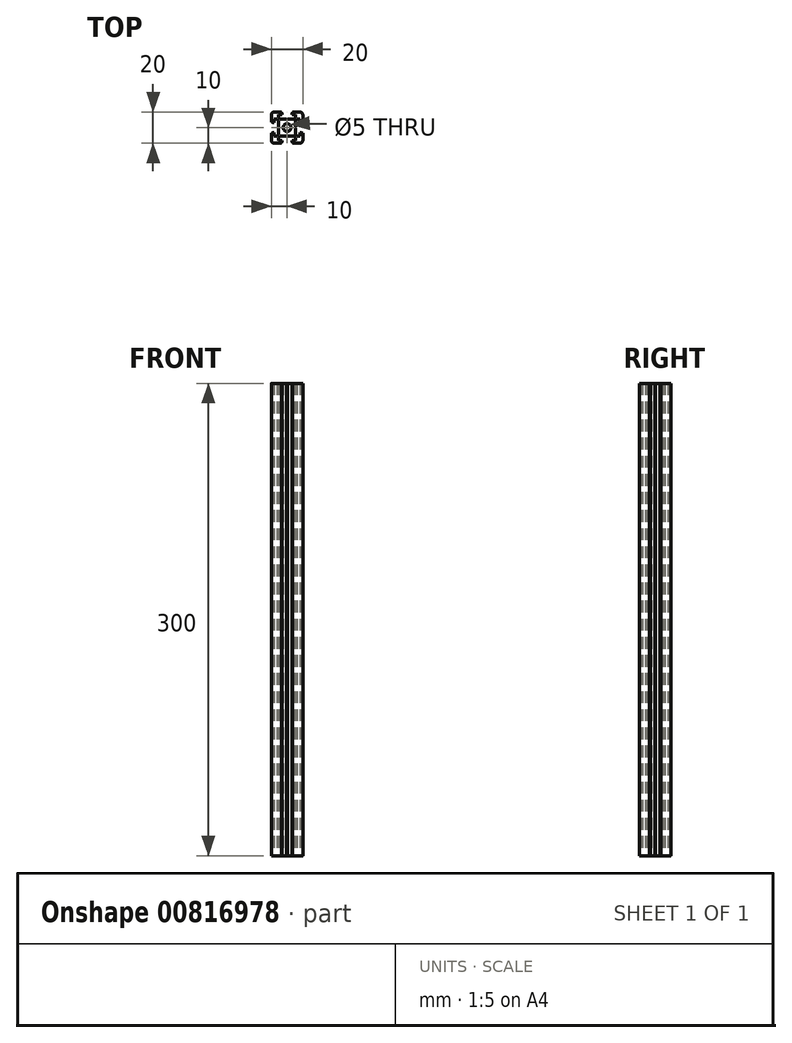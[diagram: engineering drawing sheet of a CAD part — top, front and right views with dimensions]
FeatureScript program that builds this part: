
annotation { "Feature Type Name" : "Feature", "Feature Type Description" : "" }
export const myFeature = defineFeature(function(context is Context, id is Id, definition is map)
    precondition{}
    {
        {
            var Q0;
            Q0=qCreatedBy(makeId("Top.planeOp"),FACE);
            var sketch = newSketch(context, id + "F0", { "sketchPlane" : qUnion([Q0])});
            skLineSegment(sketch, "E0.bottom", {"start": v(8, 10) * mm, "end": v(3.6, 10) * mm});
            skPoint(sketch, "E0.middle", {"position": v(0, 0) * mm});
            skLineSegment(sketch, "E1.bottom", {"start": v(4.58, 5.43) * mm, "end": v(0.25, 5.43) * mm});
            skLineSegment(sketch, "E2", {"start": v(-10, 10) * mm, "end": v(10, -10) * mm, "construction": true});
            skLineSegment(sketch, "E3", {"start": v(10, 10) * mm, "end": v(-10, -10) * mm, "construction": true});
            skLineSegment(sketch, "E4", {"start": v(-3.6, 10) * mm, "end": v(-3.6, 9.1) * mm});
            skLineSegment(sketch, "E5", {"start": v(-3.6, 9.1) * mm, "end": v(-3.1, 9.1) * mm});
            skLineSegment(sketch, "E6", {"start": v(-3.1, 9.1) * mm, "end": v(-3.1, 8.2) * mm});
            skLineSegment(sketch, "E7", {"start": v(-3.1, 8.2) * mm, "end": v(-5.45, 8.2) * mm});
            skLineSegment(sketch, "E8", {"start": v(-5.45, 8.2) * mm, "end": v(-5.45, 6.3) * mm});
            skLineSegment(sketch, "E9", {"start": v(-5.45, 6.3) * mm, "end": v(-4.58, 5.43) * mm});
            skLineSegment(sketch, "E10.MirrorCS", {"start": v(5.45, 8.2) * mm, "end": v(5.45, 6.3) * mm});
            skLineSegment(sketch, "E11.MirrorCS", {"start": v(3.1, 9.1) * mm, "end": v(3.1, 8.2) * mm});
            skLineSegment(sketch, "E12.MirrorCS", {"start": v(3.6, 10) * mm, "end": v(3.6, 9.1) * mm});
            skLineSegment(sketch, "E13.MirrorCS", {"start": v(3.1, 8.2) * mm, "end": v(5.45, 8.2) * mm});
            skLineSegment(sketch, "E14.MirrorCS", {"start": v(3.6, 9.1) * mm, "end": v(3.1, 9.1) * mm});
            skLineSegment(sketch, "E15.MirrorCS", {"start": v(5.45, 6.3) * mm, "end": v(4.58, 5.43) * mm});
            skPoint(sketch, "E16.visualSharp", {"position": v(-10, 10) * mm});
            skPoint(sketch, "E17.visualSharp", {"position": v(10, 10) * mm});
            skLineSegment(sketch, "E18.trimOffspring", {"start": v(-3.6, 10) * mm, "end": v(-8, 10) * mm});
            skLineSegment(sketch, "E19.1.0", {"start": v(-8.2, -3.1) * mm, "end": v(-8.2, -5.45) * mm});
            skLineSegment(sketch, "E19.1.2", {"start": v(-8.2, 5.45) * mm, "end": v(-6.3, 5.45) * mm});
            skLineSegment(sketch, "E19.1.3", {"start": v(-8.2, 3.1) * mm, "end": v(-8.2, 5.45) * mm});
            skPoint(sketch, "E19.1.4", {"position": v(-10, -10) * mm});
            skLineSegment(sketch, "E19.1.5", {"start": v(-9.1, -3.1) * mm, "end": v(-8.2, -3.1) * mm});
            skLineSegment(sketch, "E19.1.6", {"start": v(-6.3, 5.45) * mm, "end": v(-5.43, 4.58) * mm});
            skLineSegment(sketch, "E19.1.7", {"start": v(-5.43, 4.58) * mm, "end": v(-5.43, 0.25) * mm});
            skLineSegment(sketch, "E19.1.8", {"start": v(-8.2, -5.45) * mm, "end": v(-6.3, -5.45) * mm});
            skLineSegment(sketch, "E19.1.9", {"start": v(-9.1, 3.1) * mm, "end": v(-8.2, 3.1) * mm});
            skLineSegment(sketch, "E19.1.10", {"start": v(-6.3, -5.45) * mm, "end": v(-5.43, -4.58) * mm});
            skLineSegment(sketch, "E19.1.11", {"start": v(-10, 8) * mm, "end": v(-10, 3.6) * mm});
            skLineSegment(sketch, "E19.1.12", {"start": v(-10, -3.6) * mm, "end": v(-10, -8) * mm});
            skLineSegment(sketch, "E19.1.13", {"start": v(-10, 3.6) * mm, "end": v(-9.1, 3.6) * mm});
            skLineSegment(sketch, "E19.1.14", {"start": v(-9.1, -3.6) * mm, "end": v(-9.1, -3.1) * mm});
            skLineSegment(sketch, "E19.1.15", {"start": v(-10, -3.6) * mm, "end": v(-9.1, -3.6) * mm});
            skLineSegment(sketch, "E19.1.16", {"start": v(-9.1, 3.6) * mm, "end": v(-9.1, 3.1) * mm});
            skLineSegment(sketch, "E19.2.0", {"start": v(3.1, -8.2) * mm, "end": v(5.45, -8.2) * mm});
            skPoint(sketch, "E19.2.1", {"position": v(-10, -10) * mm});
            skLineSegment(sketch, "E19.2.2", {"start": v(-5.45, -8.2) * mm, "end": v(-5.45, -6.3) * mm});
            skLineSegment(sketch, "E19.2.3", {"start": v(-3.1, -8.2) * mm, "end": v(-5.45, -8.2) * mm});
            skPoint(sketch, "E19.2.4", {"position": v(10, -10) * mm});
            skLineSegment(sketch, "E19.2.5", {"start": v(3.1, -9.1) * mm, "end": v(3.1, -8.2) * mm});
            skLineSegment(sketch, "E19.2.6", {"start": v(-5.45, -6.3) * mm, "end": v(-4.58, -5.43) * mm});
            skLineSegment(sketch, "E19.2.7", {"start": v(-4.58, -5.43) * mm, "end": v(-0.25, -5.43) * mm});
            skLineSegment(sketch, "E19.2.8", {"start": v(5.45, -8.2) * mm, "end": v(5.45, -6.3) * mm});
            skLineSegment(sketch, "E19.2.9", {"start": v(-3.1, -9.1) * mm, "end": v(-3.1, -8.2) * mm});
            skLineSegment(sketch, "E19.2.10", {"start": v(5.45, -6.3) * mm, "end": v(4.58, -5.43) * mm});
            skLineSegment(sketch, "E19.2.11", {"start": v(-8, -10) * mm, "end": v(-3.6, -10) * mm});
            skLineSegment(sketch, "E19.2.12", {"start": v(3.6, -10) * mm, "end": v(8, -10) * mm});
            skLineSegment(sketch, "E19.2.13", {"start": v(-3.6, -10) * mm, "end": v(-3.6, -9.1) * mm});
            skLineSegment(sketch, "E19.2.14", {"start": v(3.6, -9.1) * mm, "end": v(3.1, -9.1) * mm});
            skLineSegment(sketch, "E19.2.15", {"start": v(3.6, -10) * mm, "end": v(3.6, -9.1) * mm});
            skLineSegment(sketch, "E19.2.16", {"start": v(-3.6, -9.1) * mm, "end": v(-3.1, -9.1) * mm});
            skLineSegment(sketch, "E19.3.0", {"start": v(8.2, 3.1) * mm, "end": v(8.2, 5.45) * mm});
            skPoint(sketch, "E19.3.1", {"position": v(10, -10) * mm});
            skLineSegment(sketch, "E19.3.2", {"start": v(8.2, -5.45) * mm, "end": v(6.3, -5.45) * mm});
            skLineSegment(sketch, "E19.3.3", {"start": v(8.2, -3.1) * mm, "end": v(8.2, -5.45) * mm});
            skLineSegment(sketch, "E19.3.5", {"start": v(9.1, 3.1) * mm, "end": v(8.2, 3.1) * mm});
            skLineSegment(sketch, "E19.3.6", {"start": v(6.3, -5.45) * mm, "end": v(5.43, -4.58) * mm});
            skLineSegment(sketch, "E19.3.7", {"start": v(5.43, -4.58) * mm, "end": v(5.43, -0.25) * mm});
            skLineSegment(sketch, "E19.3.8", {"start": v(8.2, 5.45) * mm, "end": v(6.3, 5.45) * mm});
            skLineSegment(sketch, "E19.3.9", {"start": v(9.1, -3.1) * mm, "end": v(8.2, -3.1) * mm});
            skLineSegment(sketch, "E19.3.10", {"start": v(6.3, 5.45) * mm, "end": v(5.43, 4.58) * mm});
            skLineSegment(sketch, "E19.3.11", {"start": v(10, -8) * mm, "end": v(10, -3.6) * mm});
            skLineSegment(sketch, "E19.3.12", {"start": v(10, 3.6) * mm, "end": v(10, 8) * mm});
            skLineSegment(sketch, "E19.3.13", {"start": v(10, -3.6) * mm, "end": v(9.1, -3.6) * mm});
            skLineSegment(sketch, "E19.3.14", {"start": v(9.1, 3.6) * mm, "end": v(9.1, 3.1) * mm});
            skLineSegment(sketch, "E19.3.15", {"start": v(10, 3.6) * mm, "end": v(9.1, 3.6) * mm});
            skLineSegment(sketch, "E19.3.16", {"start": v(9.1, -3.6) * mm, "end": v(9.1, -3.1) * mm});
            skCircle(sketch, "E20", {"center": v(0, 0) * mm, "radius": 2.5 * mm});
            skLineSegment(sketch, "E21", {"start": v(-0.25, 5.43) * mm, "end": v(0, 4.93) * mm});
            skLineSegment(sketch, "E22", {"start": v(0, 4.93) * mm, "end": v(0.25, 5.43) * mm});
            skLineSegment(sketch, "E23.trimOffspring", {"start": v(-0.25, 5.43) * mm, "end": v(-4.58, 5.43) * mm});
            skLineSegment(sketch, "E24.1.0", {"start": v(-4.93, 0) * mm, "end": v(-5.43, 0.25) * mm});
            skLineSegment(sketch, "E24.1.1", {"start": v(-5.43, -0.25) * mm, "end": v(-4.93, 0) * mm});
            skLineSegment(sketch, "E24.2.0", {"start": v(0, -4.93) * mm, "end": v(-0.25, -5.43) * mm});
            skLineSegment(sketch, "E24.2.1", {"start": v(0.25, -5.43) * mm, "end": v(0, -4.93) * mm});
            skLineSegment(sketch, "E24.3.0", {"start": v(4.93, 0) * mm, "end": v(5.43, -0.25) * mm});
            skLineSegment(sketch, "E24.3.1", {"start": v(5.43, 0.25) * mm, "end": v(4.93, 0) * mm});
            skLineSegment(sketch, "E25.trimOffspring", {"start": v(5.43, 0.25) * mm, "end": v(5.43, 4.58) * mm});
            skLineSegment(sketch, "E26.trimOffspring", {"start": v(0.25, -5.43) * mm, "end": v(4.58, -5.43) * mm});
            skLineSegment(sketch, "E27.trimOffspring", {"start": v(-5.43, -0.25) * mm, "end": v(-5.43, -4.58) * mm});
            skArc(sketch, "E28.filletArc", {"start": v(10, 8) * mm, "mid": v(9.41, 9.41) * mm, "end": v(8, 10) * mm});
            skArc(sketch, "E29.filletArc", {"start": v(8, -10) * mm, "mid": v(9.41, -9.41) * mm, "end": v(10, -8) * mm});
            skArc(sketch, "E30.filletArc", {"start": v(-10, -8) * mm, "mid": v(-9.41, -9.41) * mm, "end": v(-8, -10) * mm});
            skArc(sketch, "E31.filletArc", {"start": v(-8, 10) * mm, "mid": v(-9.41, 9.41) * mm, "end": v(-10, 8) * mm});
            skSolve(sketch);
        }
        {
            var Q0;
            Q0=makeQuery(id+"F0.imprint","IMPRINT",FACE,{"disambiguationData":[TD([[makeQuery(id+"F0.imprint","IMPRINT",EDGE,{"derivedFrom":sQuery(id+"F0.wireOp",EDGE,"E0.bottom")}),1.0]])]});
            extrude(context, id + "F1", {"entities" : qUnion([Q0]), "depth" : 300 * mm, "offsetDistance" : 25 * mm});
        }
    });
